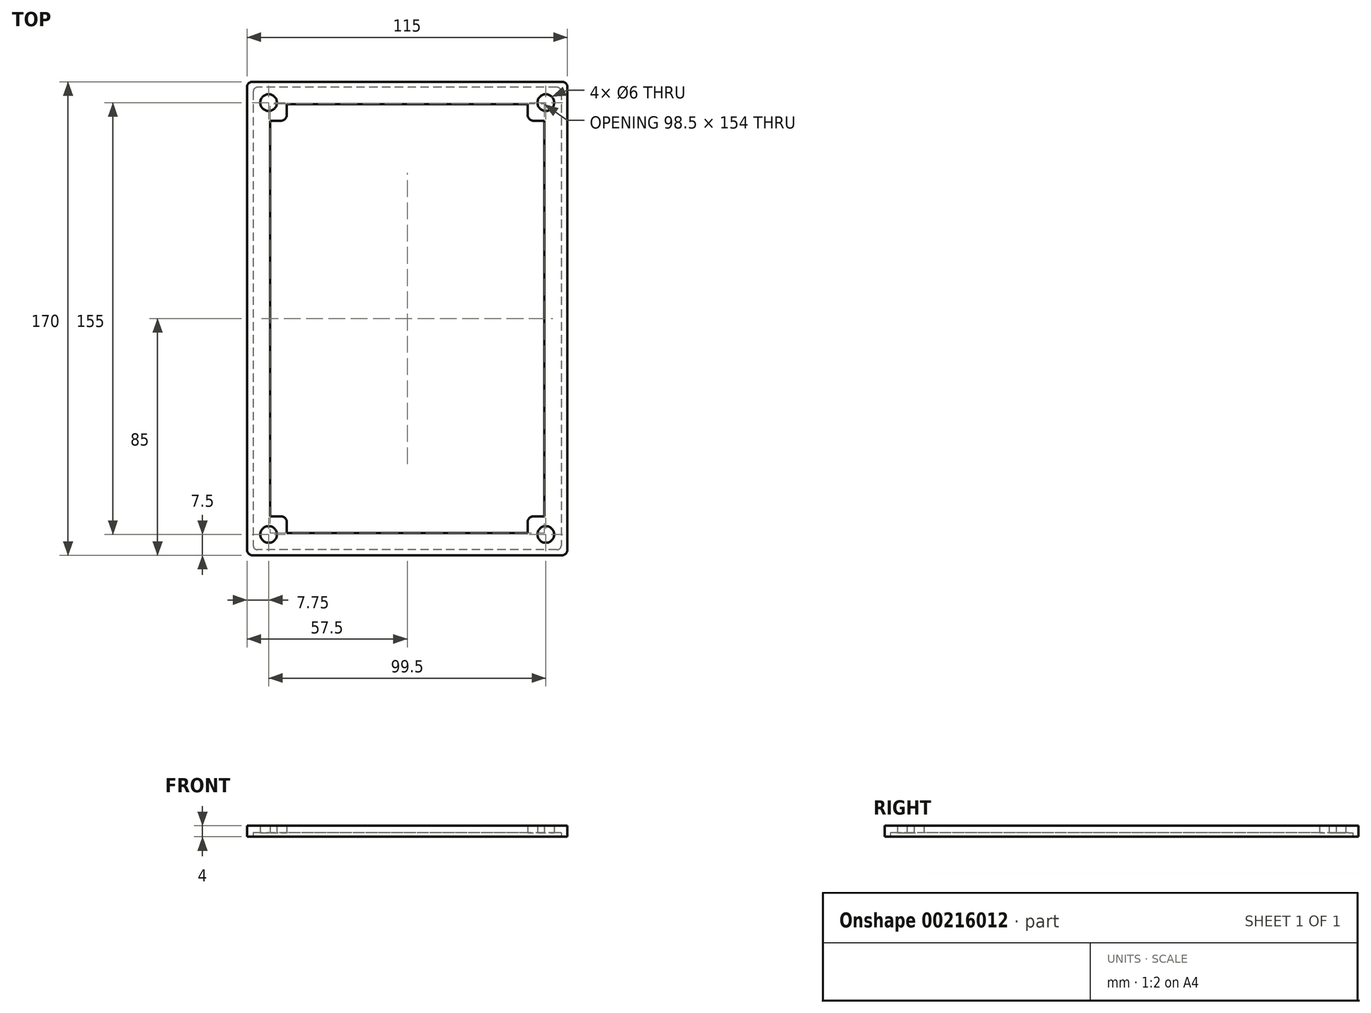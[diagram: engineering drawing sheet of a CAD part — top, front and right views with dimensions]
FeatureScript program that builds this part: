
annotation { "Feature Type Name" : "Feature", "Feature Type Description" : "" }
export const myFeature = defineFeature(function(context is Context, id is Id, definition is map)
    precondition{}
    {
        {
            var Q0;
            Q0=qCreatedBy(makeId("Top.planeOp"),FACE);
            var sketch = newSketch(context, id + "F0", { "sketchPlane" : qUnion([Q0])});
            skLineSegment(sketch, "E0.bottom", {"start": v(-57.5, 85) * mm, "end": v(57.5, 85) * mm});
            skLineSegment(sketch, "E0.top", {"start": v(-57.5, -85) * mm, "end": v(57.5, -85) * mm});
            skLineSegment(sketch, "E0.left", {"start": v(-57.5, 85) * mm, "end": v(-57.5, -85) * mm});
            skLineSegment(sketch, "E0.right", {"start": v(57.5, 85) * mm, "end": v(57.5, -85) * mm});
            skSolve(sketch);
        }
        {
            var Q0;
            Q0 = qSketchRegion(id + "F0", true);
            extrude(context, id + "F1", {"entities" : qUnion([Q0]), "depth" : 4 * mm});
        }
        {
            var Q0;
            Q0=makeQuery(id+"F1.opExtrude","CAP_FACE",FACE,{"disambiguationData":[OSD([sQuery(id+"F0.wireOp",EDGE,"E0.bottom"),sQuery(id+"F0.wireOp",EDGE,"E0.top"),sQuery(id+"F0.wireOp",EDGE,"E0.left"),sQuery(id+"F0.wireOp",EDGE,"E0.right")])],"isStart":true});
            var sketch = newSketch(context, id + "F2", { "sketchPlane" : qUnion([Q0])});
            skLineSegment(sketch, "E1.bottom", {"start": v(55.25, -83) * mm, "end": v(-55.25, -83) * mm});
            skLineSegment(sketch, "E1.top", {"start": v(55.25, 83) * mm, "end": v(-55.25, 83) * mm});
            skLineSegment(sketch, "E1.left", {"start": v(55.25, -83) * mm, "end": v(55.25, 83) * mm});
            skLineSegment(sketch, "E1.right", {"start": v(-55.25, -83) * mm, "end": v(-55.25, 83) * mm});
            skLineSegment(sketch, "E2", {"start": v(0, 0) * mm, "end": v(0, -85) * mm, "construction": true});
            skLineSegment(sketch, "E3", {"start": v(0, 0) * mm, "end": v(57.5, 0) * mm, "construction": true});
            skSolve(sketch);
        }
        {
            var Q0;
            Q0 = qSketchRegion(id + "F2", true);
            extrude(context, id + "F3", {"entities" : qUnion([Q0]), "operationType" : NewBodyOperationType.REMOVE, "oppositeDirection" : true, "depth" : 1.5 * mm});
        }
        {
            var Q0;
            Q0=makeQuery(id+"F3.boolean.opBoolean","COPY",FACE,{"derivedFrom":makeQuery(id+"F3.opExtrude","CAP_FACE",FACE,{"disambiguationData":[OSD([sQuery(id+"F2.wireOp",EDGE,"E1.bottom"),sQuery(id+"F2.wireOp",EDGE,"E1.top"),sQuery(id+"F2.wireOp",EDGE,"E1.left"),sQuery(id+"F2.wireOp",EDGE,"E1.right")])],"isStart":false})});
            var sketch = newSketch(context, id + "F4", { "sketchPlane" : qUnion([Q0])});
            skLineSegment(sketch, "E4.bottom", {"start": v(49.25, -77) * mm, "end": v(-49.25, -77) * mm});
            skLineSegment(sketch, "E4.top", {"start": v(49.25, 77) * mm, "end": v(-49.25, 77) * mm});
            skLineSegment(sketch, "E4.left", {"start": v(49.25, -77) * mm, "end": v(49.25, 77) * mm});
            skLineSegment(sketch, "E4.right", {"start": v(-49.25, -77) * mm, "end": v(-49.25, 77) * mm});
            skSolve(sketch);
        }
        {
            var Q0;
            Q0 = qSketchRegion(id + "F4", true);
            extrude(context, id + "F5", {"entities" : qUnion([Q0]), "operationType" : NewBodyOperationType.REMOVE, "endBound" : BoundingType.THROUGH_ALL, "oppositeDirection" : true, "depth" : 25 * mm});
        }
        {
            var Q0;
            Q0=makeQuery(id+"F3.boolean.opBoolean","COPY",FACE,{"derivedFrom":makeQuery(id+"F3.opExtrude","CAP_FACE",FACE,{"disambiguationData":[OSD([sQuery(id+"F2.wireOp",EDGE,"E1.bottom"),sQuery(id+"F2.wireOp",EDGE,"E1.top"),sQuery(id+"F2.wireOp",EDGE,"E1.left"),sQuery(id+"F2.wireOp",EDGE,"E1.right")])],"isStart":false})});
            var sketch = newSketch(context, id + "F6", { "sketchPlane" : qUnion([Q0])});
            skLineSegment(sketch, "E5.bottom", {"start": v(54.75, -82.5) * mm, "end": v(-54.75, -82.5) * mm});
            skLineSegment(sketch, "E5.top", {"start": v(54.75, 82.5) * mm, "end": v(-54.75, 82.5) * mm});
            skLineSegment(sketch, "E5.left", {"start": v(54.75, -82.5) * mm, "end": v(54.75, 82.5) * mm});
            skLineSegment(sketch, "E5.right", {"start": v(-54.75, -82.5) * mm, "end": v(-54.75, 82.5) * mm});
            skCircle(sketch, "E6", {"center": v(49.75, -77.5) * mm, "radius": 2.5 * mm});
            skSolve(sketch);
        }
        {
            var Q0;
            Q0=makeQuery(id+"F3.boolean.opBoolean","COPY",FACE,{"derivedFrom":makeQuery(id+"F3.opExtrude","CAP_FACE",FACE,{"disambiguationData":[OSD([sQuery(id+"F2.wireOp",EDGE,"E1.bottom"),sQuery(id+"F2.wireOp",EDGE,"E1.top"),sQuery(id+"F2.wireOp",EDGE,"E1.left"),sQuery(id+"F2.wireOp",EDGE,"E1.right")])],"isStart":false})});
            var sketch = newSketch(context, id + "F7", { "sketchPlane" : qUnion([Q0])});
            skLineSegment(sketch, "E7.bottom", {"start": v(49.25, -77) * mm, "end": v(43.25, -77) * mm});
            skLineSegment(sketch, "E7.top", {"start": v(49.25, -71) * mm, "end": v(43.25, -71) * mm});
            skLineSegment(sketch, "E7.left", {"start": v(49.25, -77) * mm, "end": v(49.25, -71) * mm});
            skLineSegment(sketch, "E7.right", {"start": v(43.25, -77) * mm, "end": v(43.25, -71) * mm});
            skLineSegment(sketch, "E8", {"start": v(49.25, -77) * mm, "end": v(55.25, -77) * mm, "construction": true});
            skLineSegment(sketch, "E9", {"start": v(49.25, -77) * mm, "end": v(49.25, -83) * mm, "construction": true});
            skLineSegment(sketch, "E10.bottom", {"start": v(-43.25, -77) * mm, "end": v(-49.25, -77) * mm});
            skLineSegment(sketch, "E10.top", {"start": v(-43.25, -71) * mm, "end": v(-49.25, -71) * mm});
            skLineSegment(sketch, "E10.left", {"start": v(-43.25, -77) * mm, "end": v(-43.25, -71) * mm});
            skLineSegment(sketch, "E10.right", {"start": v(-49.25, -77) * mm, "end": v(-49.25, -71) * mm});
            skLineSegment(sketch, "E11.bottom", {"start": v(-49.25, 77) * mm, "end": v(-43.25, 77) * mm});
            skLineSegment(sketch, "E11.top", {"start": v(-49.25, 71) * mm, "end": v(-43.25, 71) * mm});
            skLineSegment(sketch, "E11.left", {"start": v(-49.25, 77) * mm, "end": v(-49.25, 71) * mm});
            skLineSegment(sketch, "E11.right", {"start": v(-43.25, 77) * mm, "end": v(-43.25, 71) * mm});
            skLineSegment(sketch, "E12.bottom", {"start": v(49.25, 77) * mm, "end": v(43.25, 77) * mm});
            skLineSegment(sketch, "E12.top", {"start": v(49.25, 71) * mm, "end": v(43.25, 71) * mm});
            skLineSegment(sketch, "E12.left", {"start": v(49.25, 77) * mm, "end": v(49.25, 71) * mm});
            skLineSegment(sketch, "E12.right", {"start": v(43.25, 77) * mm, "end": v(43.25, 71) * mm});
            skSolve(sketch);
        }
        {
            var Q0;
            Q0 = qSketchRegion(id + "F7", true);
            var Q1;
            Q1=makeQuery(id+"F1.opExtrude","CAP_FACE",FACE,{"disambiguationData":[OSD([sQuery(id+"F0.wireOp",EDGE,"E0.bottom"),sQuery(id+"F0.wireOp",EDGE,"E0.top"),sQuery(id+"F0.wireOp",EDGE,"E0.left"),sQuery(id+"F0.wireOp",EDGE,"E0.right")])],"isStart":false});
            extrude(context, id + "F8", {"entities" : qUnion([Q0]), "operationType" : NewBodyOperationType.ADD, "endBound" : BoundingType.UP_TO_SURFACE, "oppositeDirection" : true, "endBoundEntityFace" : qUnion([Q1]), "depth" : 25 * mm});
        }
        {
            var Q0;
            Q0=makeQuery(id+"F6.imprint","IMPRINT",FACE,{"disambiguationData":[TD([[makeQuery(id+"F6.imprint","IMPRINT",EDGE,{"derivedFrom":sQuery(id+"F6.wireOp",EDGE,"E5.bottom")}),-1.0]])]});
            var sketch = newSketch(context, id + "F9", { "sketchPlane" : qUnion([Q0])});
            skCircle(sketch, "E13", {"center": v(49.75, -77.5) * mm, "radius": 3 * mm});
            skCircle(sketch, "E14", {"center": v(-49.75, -77.5) * mm, "radius": 3 * mm});
            skCircle(sketch, "E15", {"center": v(-49.75, 77.5) * mm, "radius": 3 * mm});
            skCircle(sketch, "E16", {"center": v(49.75, 77.5) * mm, "radius": 3 * mm});
            skLineSegment(sketch, "E17", {"start": v(49.75, -77.5) * mm, "end": v(-49.75, -77.5) * mm, "construction": true});
            skLineSegment(sketch, "E18", {"start": v(49.75, -77.5) * mm, "end": v(49.75, 77.5) * mm, "construction": true});
            skLineSegment(sketch, "E19", {"start": v(49.75, 77.5) * mm, "end": v(-49.75, 77.5) * mm, "construction": true});
            skSolve(sketch);
        }
        {
            var Q0;
            Q0 = qSketchRegion(id + "F9", true);
            extrude(context, id + "F10", {"entities" : qUnion([Q0]), "operationType" : NewBodyOperationType.REMOVE, "endBound" : BoundingType.THROUGH_ALL, "oppositeDirection" : true, "depth" : 25 * mm});
        }
        {
            var Q0;
            Q0=makeQuery(id+"F8.opExtrude","SWEPT_EDGE",EDGE,{"disambiguationData":[OSD([sQuery(id+"F4.wireOp",EDGE,"E4.bottom"),sQuery(id+"F7.wireOp",EDGE,"E10.bottom"),sQuery(id+"F7.wireOp",EDGE,"E10.left")])]});
            var Q1;
            Q1=makeQuery(id+"F8.opExtrude","SWEPT_EDGE",EDGE,{"disambiguationData":[OSD([sQuery(id+"F7.wireOp",EDGE,"E10.top"),sQuery(id+"F7.wireOp",EDGE,"E10.left")])]});
            var Q2;
            Q2=makeQuery(id+"F8.opExtrude","SWEPT_EDGE",EDGE,{"disambiguationData":[OSD([sQuery(id+"F4.wireOp",EDGE,"E4.right"),sQuery(id+"F7.wireOp",EDGE,"E10.top"),sQuery(id+"F7.wireOp",EDGE,"E10.right")])]});
            var Q3;
            Q3=makeQuery(id+"F8.opExtrude","SWEPT_EDGE",EDGE,{"disambiguationData":[OSD([sQuery(id+"F4.wireOp",EDGE,"E4.left"),sQuery(id+"F7.wireOp",EDGE,"E7.top"),sQuery(id+"F7.wireOp",EDGE,"E7.left")])]});
            var Q4;
            Q4=makeQuery(id+"F8.opExtrude","SWEPT_EDGE",EDGE,{"disambiguationData":[OSD([sQuery(id+"F7.wireOp",EDGE,"E7.top"),sQuery(id+"F7.wireOp",EDGE,"E7.right")])]});
            var Q5;
            Q5=makeQuery(id+"F8.opExtrude","SWEPT_EDGE",EDGE,{"disambiguationData":[OSD([sQuery(id+"F4.wireOp",EDGE,"E4.bottom"),sQuery(id+"F7.wireOp",EDGE,"E7.bottom"),sQuery(id+"F7.wireOp",EDGE,"E7.right")])]});
            var Q6;
            Q6=makeQuery(id+"F8.opExtrude","SWEPT_EDGE",EDGE,{"disambiguationData":[OSD([sQuery(id+"F4.wireOp",EDGE,"E4.left"),sQuery(id+"F7.wireOp",EDGE,"E12.top"),sQuery(id+"F7.wireOp",EDGE,"E12.left")])]});
            var Q7;
            Q7=makeQuery(id+"F8.opExtrude","SWEPT_EDGE",EDGE,{"disambiguationData":[OSD([sQuery(id+"F7.wireOp",EDGE,"E12.top"),sQuery(id+"F7.wireOp",EDGE,"E12.right")])]});
            var Q8;
            Q8=makeQuery(id+"F8.opExtrude","SWEPT_EDGE",EDGE,{"disambiguationData":[OSD([sQuery(id+"F4.wireOp",EDGE,"E4.top"),sQuery(id+"F7.wireOp",EDGE,"E12.bottom"),sQuery(id+"F7.wireOp",EDGE,"E12.right")])]});
            var Q9;
            Q9=makeQuery(id+"F8.opExtrude","SWEPT_EDGE",EDGE,{"disambiguationData":[OSD([sQuery(id+"F4.wireOp",EDGE,"E4.top"),sQuery(id+"F7.wireOp",EDGE,"E11.bottom"),sQuery(id+"F7.wireOp",EDGE,"E11.right")])]});
            var Q10;
            Q10=makeQuery(id+"F8.opExtrude","SWEPT_EDGE",EDGE,{"disambiguationData":[OSD([sQuery(id+"F7.wireOp",EDGE,"E11.top"),sQuery(id+"F7.wireOp",EDGE,"E11.right")])]});
            var Q11;
            Q11=makeQuery(id+"F8.opExtrude","SWEPT_EDGE",EDGE,{"disambiguationData":[OSD([sQuery(id+"F4.wireOp",EDGE,"E4.right"),sQuery(id+"F7.wireOp",EDGE,"E11.top"),sQuery(id+"F7.wireOp",EDGE,"E11.left")])]});
            fillet(context, id + "F11", {"entities" : qUnion([Q0, Q1, Q2, Q3, Q4, Q5, Q6, Q7, Q8, Q9, Q10, Q11]), "radius" : 2 * mm, "tangentPropagation" : true, "allowEdgeOverflow" : false});
        }
        {
            var Q0;
            Q0=makeQuery(id+"F1.opExtrude","SWEPT_EDGE",EDGE,{"disambiguationData":[OSD([sQuery(id+"F0.wireOp",EDGE,"E0.bottom"),sQuery(id+"F0.wireOp",EDGE,"E0.left")])]});
            var Q1;
            Q1=makeQuery(id+"F1.opExtrude","SWEPT_EDGE",EDGE,{"disambiguationData":[OSD([sQuery(id+"F0.wireOp",EDGE,"E0.bottom"),sQuery(id+"F0.wireOp",EDGE,"E0.right")])]});
            var Q2;
            Q2=makeQuery(id+"F1.opExtrude","SWEPT_EDGE",EDGE,{"disambiguationData":[OSD([sQuery(id+"F0.wireOp",EDGE,"E0.top"),sQuery(id+"F0.wireOp",EDGE,"E0.right")])]});
            var Q3;
            Q3=makeQuery(id+"F1.opExtrude","SWEPT_EDGE",EDGE,{"disambiguationData":[OSD([sQuery(id+"F0.wireOp",EDGE,"E0.top"),sQuery(id+"F0.wireOp",EDGE,"E0.left")])]});
            fillet(context, id + "F12", {"entities" : qUnion([Q0, Q1, Q2, Q3]), "radius" : 2 * mm, "tangentPropagation" : true, "allowEdgeOverflow" : false});
        }
        {
            var Q0;
            Q0=makeQuery(id+"F3.boolean.opBoolean","COPY",EDGE,{"derivedFrom":makeQuery(id+"F3.opExtrude","SWEPT_EDGE",EDGE,{"disambiguationData":[OSD([sQuery(id+"F2.wireOp",EDGE,"E1.bottom"),sQuery(id+"F2.wireOp",EDGE,"E1.left")])]})});
            var Q1;
            Q1=makeQuery(id+"F3.boolean.opBoolean","COPY",EDGE,{"derivedFrom":makeQuery(id+"F3.opExtrude","SWEPT_EDGE",EDGE,{"disambiguationData":[OSD([sQuery(id+"F2.wireOp",EDGE,"E1.bottom"),sQuery(id+"F2.wireOp",EDGE,"E1.right")])]})});
            var Q2;
            Q2=makeQuery(id+"F3.boolean.opBoolean","COPY",EDGE,{"derivedFrom":makeQuery(id+"F3.opExtrude","SWEPT_EDGE",EDGE,{"disambiguationData":[OSD([sQuery(id+"F2.wireOp",EDGE,"E1.top"),sQuery(id+"F2.wireOp",EDGE,"E1.right")])]})});
            var Q3;
            Q3=makeQuery(id+"F3.boolean.opBoolean","COPY",EDGE,{"derivedFrom":makeQuery(id+"F3.opExtrude","SWEPT_EDGE",EDGE,{"disambiguationData":[OSD([sQuery(id+"F2.wireOp",EDGE,"E1.top"),sQuery(id+"F2.wireOp",EDGE,"E1.left")])]})});
            fillet(context, id + "F13", {"entities" : qUnion([Q0, Q1, Q2, Q3]), "radius" : 1.5 * mm, "tangentPropagation" : true, "allowEdgeOverflow" : false});
        }
    });
